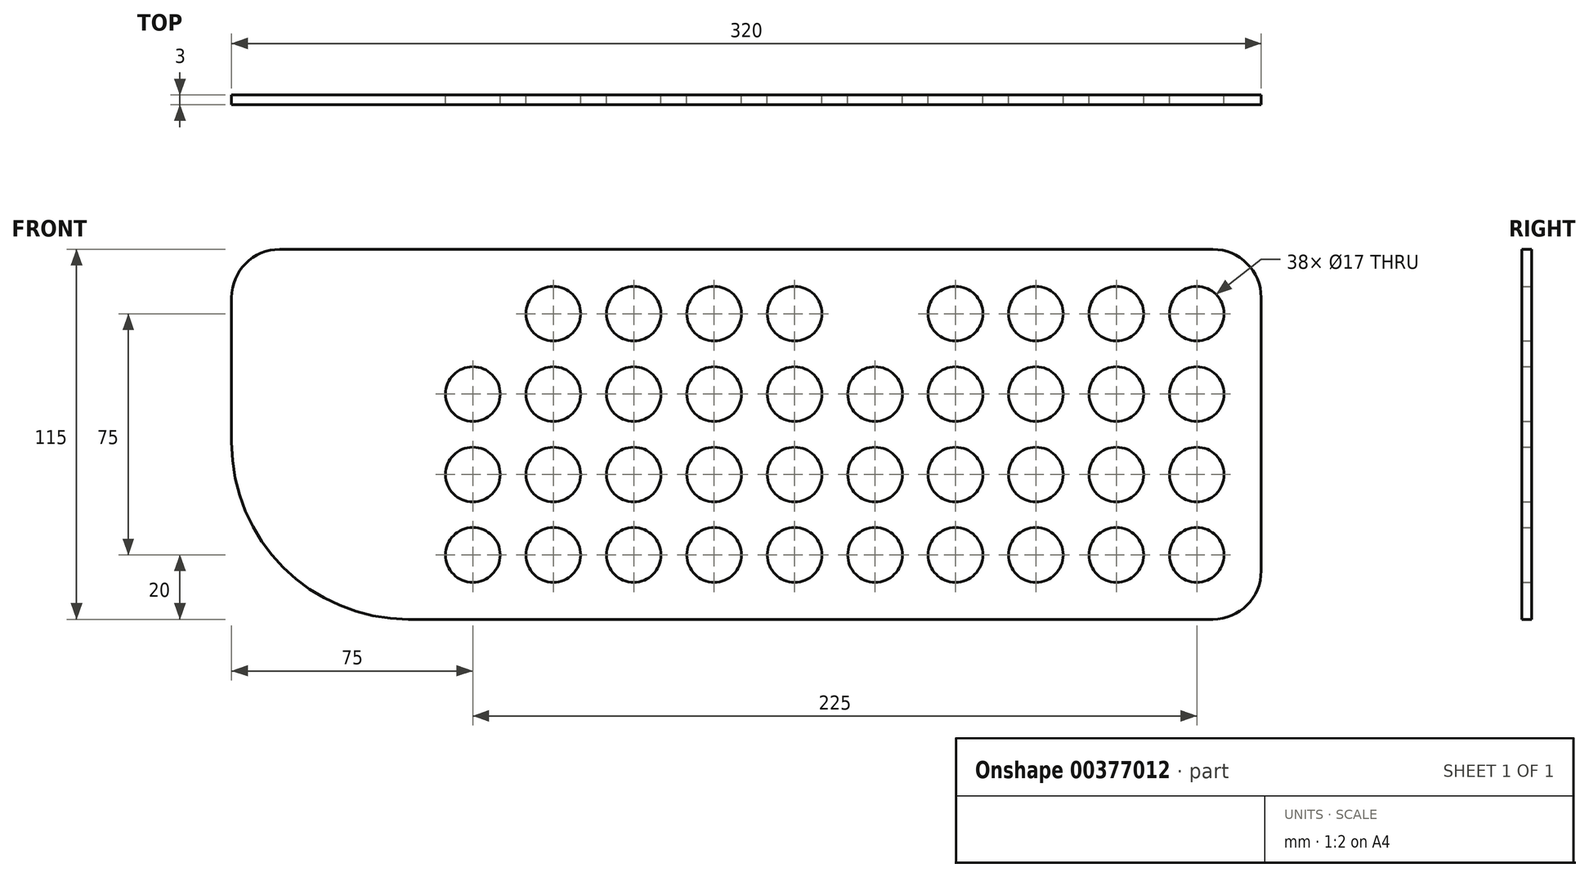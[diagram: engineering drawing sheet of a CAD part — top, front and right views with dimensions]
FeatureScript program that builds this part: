
annotation { "Feature Type Name" : "Feature", "Feature Type Description" : "" }
export const myFeature = defineFeature(function(context is Context, id is Id, definition is map)
    precondition{}
    {
        {
            var Q0;
            Q0=qCreatedBy(makeId("Front.planeOp"),FACE);
            var sketch = newSketch(context, id + "F0", { "sketchPlane" : qUnion([Q0])});
            skLineSegment(sketch, "E0.bottom", {"start": v(55, 0) * mm, "end": v(305, 0) * mm});
            skLineSegment(sketch, "E0.top", {"start": v(15, 115) * mm, "end": v(305, 115) * mm});
            skLineSegment(sketch, "E0.left", {"start": v(0, 55) * mm, "end": v(0, 100) * mm});
            skLineSegment(sketch, "E0.right", {"start": v(320, 15) * mm, "end": v(320, 100) * mm});
            skPoint(sketch, "E1.visualSharp", {"position": v(0, 115) * mm});
            skArc(sketch, "E1.filletArc", {"start": v(15, 115) * mm, "mid": v(4.4, 110.6) * mm, "end": v(0, 100) * mm});
            skPoint(sketch, "E2.visualSharp", {"position": v(320, 115) * mm});
            skArc(sketch, "E2.filletArc", {"start": v(320, 100) * mm, "mid": v(315.6, 110.6) * mm, "end": v(305, 115) * mm});
            skPoint(sketch, "E3.visualSharp", {"position": v(320, 0) * mm});
            skArc(sketch, "E3.filletArc", {"start": v(305, 0) * mm, "mid": v(315.6, 4.4) * mm, "end": v(320, 15) * mm});
            skPoint(sketch, "E4.visualSharp", {"position": v(0, 0) * mm});
            skArc(sketch, "E4.filletArc", {"start": v(0, 55) * mm, "mid": v(16.1, 16.1) * mm, "end": v(55, 0) * mm});
            skCircle(sketch, "E5", {"center": v(300, 20) * mm, "radius": 8.5 * mm});
            skCircle(sketch, "E6.0.1.0", {"center": v(300, 45) * mm, "radius": 8.5 * mm});
            skCircle(sketch, "E6.0.2.0", {"center": v(300, 70) * mm, "radius": 8.5 * mm});
            skCircle(sketch, "E6.0.3.0", {"center": v(300, 95) * mm, "radius": 8.5 * mm});
            skCircle(sketch, "E6.1.0.0", {"center": v(275, 20) * mm, "radius": 8.5 * mm});
            skCircle(sketch, "E6.1.1.0", {"center": v(275, 45) * mm, "radius": 8.5 * mm});
            skCircle(sketch, "E6.1.2.0", {"center": v(275, 70) * mm, "radius": 8.5 * mm});
            skCircle(sketch, "E6.1.3.0", {"center": v(275, 95) * mm, "radius": 8.5 * mm});
            skCircle(sketch, "E6.2.0.0", {"center": v(250, 20) * mm, "radius": 8.5 * mm});
            skCircle(sketch, "E6.2.1.0", {"center": v(250, 45) * mm, "radius": 8.5 * mm});
            skCircle(sketch, "E6.2.2.0", {"center": v(250, 70) * mm, "radius": 8.5 * mm});
            skCircle(sketch, "E6.2.3.0", {"center": v(250, 95) * mm, "radius": 8.5 * mm});
            skCircle(sketch, "E6.3.0.0", {"center": v(225, 20) * mm, "radius": 8.5 * mm});
            skCircle(sketch, "E6.3.1.0", {"center": v(225, 45) * mm, "radius": 8.5 * mm});
            skCircle(sketch, "E6.3.2.0", {"center": v(225, 70) * mm, "radius": 8.5 * mm});
            skCircle(sketch, "E6.3.3.0", {"center": v(225, 95) * mm, "radius": 8.5 * mm});
            skCircle(sketch, "E6.4.0.0", {"center": v(200, 20) * mm, "radius": 8.5 * mm});
            skCircle(sketch, "E6.4.1.0", {"center": v(200, 45) * mm, "radius": 8.5 * mm});
            skCircle(sketch, "E6.4.2.0", {"center": v(200, 70) * mm, "radius": 8.5 * mm});
            skCircle(sketch, "E6.5.0.0", {"center": v(175, 20) * mm, "radius": 8.5 * mm});
            skCircle(sketch, "E6.5.1.0", {"center": v(175, 45) * mm, "radius": 8.5 * mm});
            skCircle(sketch, "E6.5.2.0", {"center": v(175, 70) * mm, "radius": 8.5 * mm});
            skCircle(sketch, "E6.5.3.0", {"center": v(175, 95) * mm, "radius": 8.5 * mm});
            skCircle(sketch, "E6.6.0.0", {"center": v(150, 20) * mm, "radius": 8.5 * mm});
            skCircle(sketch, "E6.6.1.0", {"center": v(150, 45) * mm, "radius": 8.5 * mm});
            skCircle(sketch, "E6.6.2.0", {"center": v(150, 70) * mm, "radius": 8.5 * mm});
            skCircle(sketch, "E6.6.3.0", {"center": v(150, 95) * mm, "radius": 8.5 * mm});
            skCircle(sketch, "E6.7.0.0", {"center": v(125, 20) * mm, "radius": 8.5 * mm});
            skCircle(sketch, "E6.7.1.0", {"center": v(125, 45) * mm, "radius": 8.5 * mm});
            skCircle(sketch, "E6.7.2.0", {"center": v(125, 70) * mm, "radius": 8.5 * mm});
            skCircle(sketch, "E6.7.3.0", {"center": v(125, 95) * mm, "radius": 8.5 * mm});
            skCircle(sketch, "E6.8.0.0", {"center": v(100, 20) * mm, "radius": 8.5 * mm});
            skCircle(sketch, "E6.8.1.0", {"center": v(100, 45) * mm, "radius": 8.5 * mm});
            skCircle(sketch, "E6.8.2.0", {"center": v(100, 70) * mm, "radius": 8.5 * mm});
            skCircle(sketch, "E6.8.3.0", {"center": v(100, 95) * mm, "radius": 8.5 * mm});
            skCircle(sketch, "E6.9.0.0", {"center": v(75, 20) * mm, "radius": 8.5 * mm});
            skCircle(sketch, "E6.9.1.0", {"center": v(75, 45) * mm, "radius": 8.5 * mm});
            skCircle(sketch, "E6.9.2.0", {"center": v(75, 70) * mm, "radius": 8.5 * mm});
            skLineSegment(sketch, "E6.direction1", {"start": v(300, 20) * mm, "end": v(275, 20) * mm, "construction": true});
            skLineSegment(sketch, "E6.direction2", {"start": v(300, 20) * mm, "end": v(300, 45) * mm, "construction": true});
            skSolve(sketch);
        }
        {
            var Q0;
            Q0=makeQuery(id+"F0.imprint","IMPRINT",FACE,{"disambiguationData":[TD([[makeQuery(id+"F0.imprint","IMPRINT",EDGE,{"derivedFrom":sQuery(id+"F0.wireOp",EDGE,"E0.bottom")}),1.0]])]});
            extrude(context, id + "F1", {"entities" : qUnion([Q0]), "depth" : 3 * mm});
        }
    });
